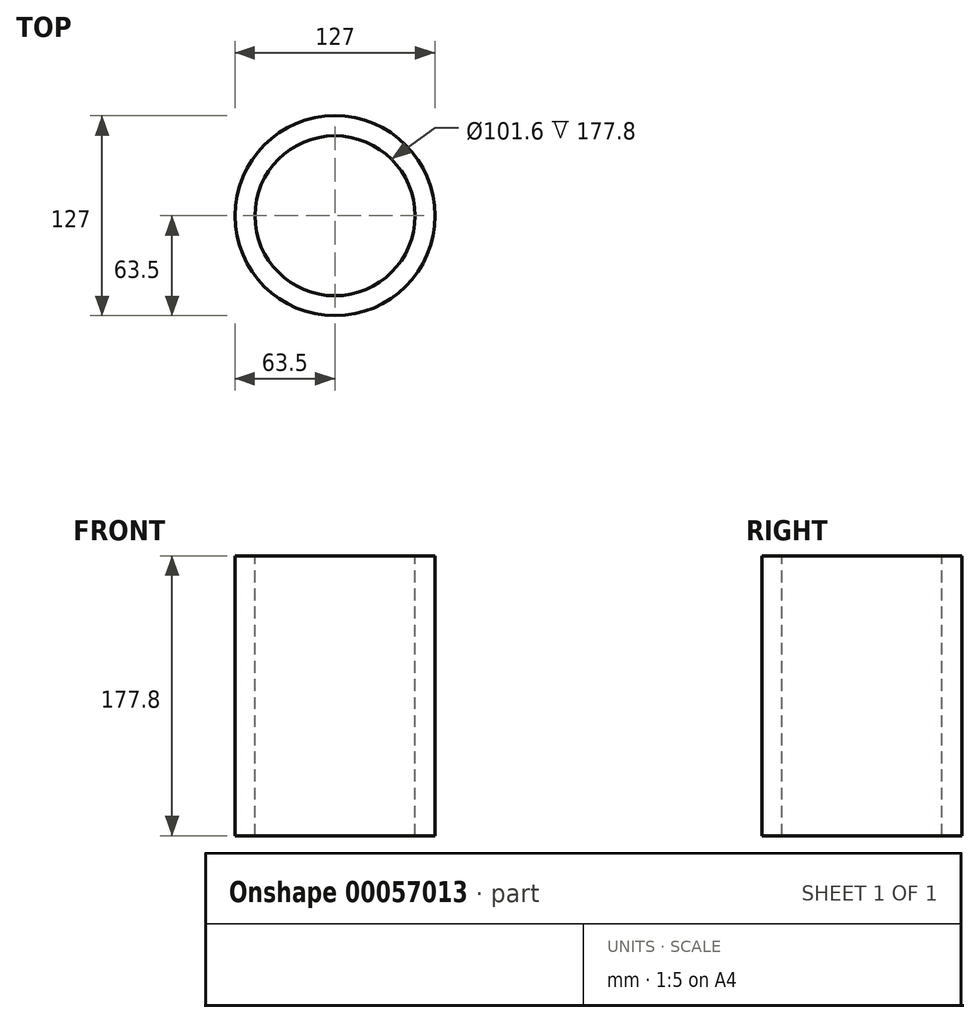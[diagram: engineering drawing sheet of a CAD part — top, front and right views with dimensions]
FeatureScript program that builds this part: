
annotation { "Feature Type Name" : "Feature", "Feature Type Description" : "" }
export const myFeature = defineFeature(function(context is Context, id is Id, definition is map)
    precondition{}
    {
        {
            var Q0;
            Q0=qCreatedBy(makeId("Top.planeOp"),FACE);
            var sketch = newSketch(context, id + "F0", { "sketchPlane" : qUnion([Q0])});
            skCircle(sketch, "E0", {"center": v(0, 0) * mm, "radius": 63.5 * mm});
            skSolve(sketch);
        }
        {
            var Q0;
            Q0=makeQuery(id+"F0.imprint","IMPRINT",FACE,{"disambiguationData":[TD([[makeQuery(id+"F0.imprint","IMPRINT",EDGE,{"derivedFrom":sQuery(id+"F0.wireOp",EDGE,"E0")}),1.0]])]});
            extrude(context, id + "F1", {"entities" : qUnion([Q0]), "oppositeDirection" : true, "depth" : 177.8 * mm});
        }
        {
            var Q0;
            Q0=makeQuery(id+"F1.opExtrude","CAP_FACE",FACE,{"disambiguationData":[OSD([sQuery(id+"F0.wireOp",EDGE,"E0")])],"isStart":true});
            var Q1;
            Q1=makeQuery(id+"F1.opExtrude","CAP_FACE",FACE,{"disambiguationData":[OSD([sQuery(id+"F0.wireOp",EDGE,"E0")])],"isStart":false});
            shell(context, id + "F2", {"entities" : qUnion([Q0, Q1]), "thickness" : 12.7 * mm});
        }
    });
